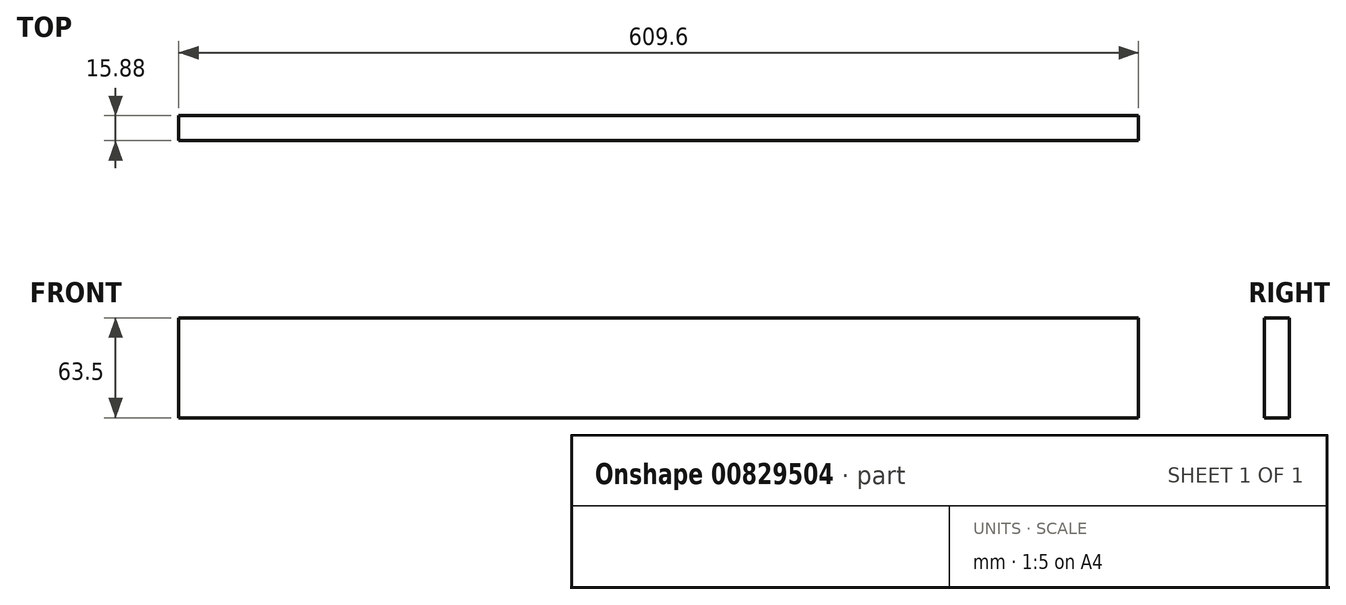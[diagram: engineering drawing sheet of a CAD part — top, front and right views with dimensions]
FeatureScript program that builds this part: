
annotation { "Feature Type Name" : "Feature", "Feature Type Description" : "" }
export const myFeature = defineFeature(function(context is Context, id is Id, definition is map)
    precondition{}
    {
        {
            var Q0;
            Q0=qCreatedBy(makeId("Right.planeOp"),FACE);
            var sketch = newSketch(context, id + "F0", { "sketchPlane" : qUnion([Q0])});
            skLineSegment(sketch, "E0.bottom", {"start": v(0, 0) * mm, "end": v(15.88, 0) * mm});
            skLineSegment(sketch, "E0.top", {"start": v(0, -63.5) * mm, "end": v(15.88, -63.5) * mm});
            skLineSegment(sketch, "E0.left", {"start": v(0, 0) * mm, "end": v(0, -63.5) * mm});
            skLineSegment(sketch, "E0.right", {"start": v(15.88, 0) * mm, "end": v(15.88, -63.5) * mm});
            skSolve(sketch);
        }
        {
            var Q0;
            Q0 = qSketchRegion(id + "F0", true);
            extrude(context, id + "F1", {"entities" : qUnion([Q0]), "depth" : 609.6 * mm, "offsetDistance" : 25.4 * mm});
        }
    });
